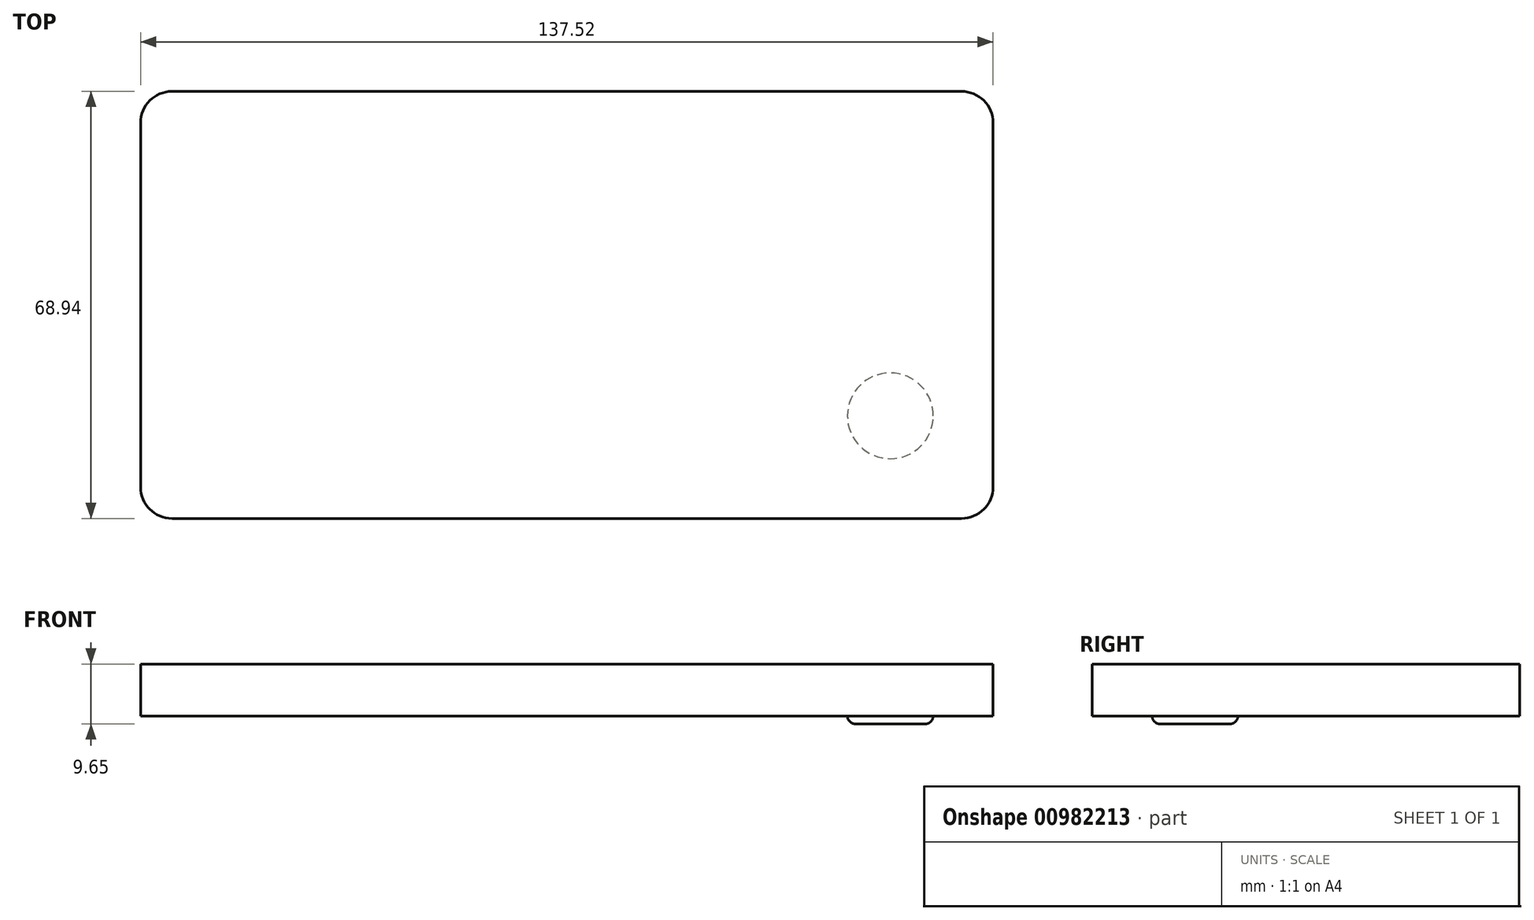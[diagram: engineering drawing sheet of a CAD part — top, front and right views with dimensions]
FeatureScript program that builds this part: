
annotation { "Feature Type Name" : "Feature", "Feature Type Description" : "" }
export const myFeature = defineFeature(function(context is Context, id is Id, definition is map)
    precondition{}
    {
        {
            var Q0;
            Q0=qCreatedBy(makeId("Top.planeOp"),FACE);
            var sketch = newSketch(context, id + "F0", { "sketchPlane" : qUnion([Q0])});
            skLineSegment(sketch, "E0.bottom", {"start": v(68.76, -34.47) * mm, "end": v(-68.76, -34.47) * mm});
            skLineSegment(sketch, "E0.top", {"start": v(68.76, 34.47) * mm, "end": v(-68.76, 34.47) * mm});
            skLineSegment(sketch, "E0.left", {"start": v(68.76, -34.47) * mm, "end": v(68.76, 34.47) * mm});
            skLineSegment(sketch, "E0.right", {"start": v(-68.76, -34.47) * mm, "end": v(-68.76, 34.47) * mm});
            skPoint(sketch, "E0.middle", {"position": v(0, 0) * mm});
            skSolve(sketch);
        }
        {
            var Q0;
            Q0=makeQuery(id+"F0.imprint","IMPRINT",FACE,{"disambiguationData":[TD([[makeQuery(id+"F0.imprint","IMPRINT",EDGE,{"derivedFrom":sQuery(id+"F0.wireOp",EDGE,"E0.bottom")}),-1.0]])]});
            extrude(context, id + "F1", {"entities" : qUnion([Q0]), "depth" : 8.38 * mm, "offsetDistance" : 25.4 * mm});
        }
        {
            var Q0;
            Q0=makeQuery(id+"F1.opExtrude","SWEPT_EDGE",EDGE,{"disambiguationData":[OSD([sQuery(id+"F0.wireOp",EDGE,"E0.top"),sQuery(id+"F0.wireOp",EDGE,"E0.right")])]});
            var Q1;
            Q1=makeQuery(id+"F1.opExtrude","SWEPT_EDGE",EDGE,{"disambiguationData":[OSD([sQuery(id+"F0.wireOp",EDGE,"E0.bottom"),sQuery(id+"F0.wireOp",EDGE,"E0.right")])]});
            var Q2;
            Q2=makeQuery(id+"F1.opExtrude","SWEPT_EDGE",EDGE,{"disambiguationData":[OSD([sQuery(id+"F0.wireOp",EDGE,"E0.bottom"),sQuery(id+"F0.wireOp",EDGE,"E0.left")])]});
            var Q3;
            Q3=makeQuery(id+"F1.opExtrude","SWEPT_EDGE",EDGE,{"disambiguationData":[OSD([sQuery(id+"F0.wireOp",EDGE,"E0.top"),sQuery(id+"F0.wireOp",EDGE,"E0.left")])]});
            fillet(context, id + "F2", {"entities" : qUnion([Q0, Q1, Q2, Q3]), "radius" : 5.08 * mm, "tangentPropagation" : true, "allowEdgeOverflow" : false});
        }
        {
            var Q0;
            Q0=makeQuery(id+"F1.opExtrude","CAP_FACE",FACE,{"disambiguationData":[OSD([sQuery(id+"F0.wireOp",EDGE,"E0.bottom"),sQuery(id+"F0.wireOp",EDGE,"E0.top"),sQuery(id+"F0.wireOp",EDGE,"E0.left"),sQuery(id+"F0.wireOp",EDGE,"E0.right")])],"isStart":true});
            var sketch = newSketch(context, id + "F3", { "sketchPlane" : qUnion([Q0])});
            skCircle(sketch, "E1", {"center": v(52.18, 17.9) * mm, "radius": 6.92 * mm});
            skSolve(sketch);
        }
        {
            var Q0;
            Q0=makeQuery(id+"F3.imprint","IMPRINT",FACE,{"disambiguationData":[TD([[makeQuery(id+"F3.imprint","IMPRINT",EDGE,{"derivedFrom":sQuery(id+"F3.wireOp",EDGE,"E1")}),1.0]])]});
            extrude(context, id + "F4", {"entities" : qUnion([Q0]), "operationType" : NewBodyOperationType.ADD, "depth" : 1.27 * mm, "offsetDistance" : 25.4 * mm});
        }
        {
            var Q0;
            Q0=makeQuery(id+"F4.opExtrude","CAP_EDGE",EDGE,{"disambiguationData":[OSD([sQuery(id+"F3.wireOp",EDGE,"E1")])],"isStart":false});
            fillet(context, id + "F5", {"entities" : qUnion([Q0]), "radius" : 1.27 * mm, "tangentPropagation" : true, "allowEdgeOverflow" : false});
        }
    });
